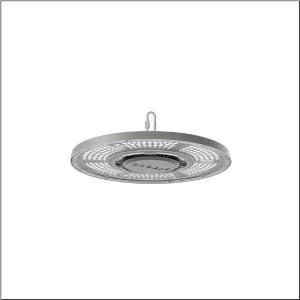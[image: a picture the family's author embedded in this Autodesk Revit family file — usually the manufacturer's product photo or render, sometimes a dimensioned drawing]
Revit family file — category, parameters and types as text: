
# Revit family: highbay_31-s_51hc42da4fmb
name_source: partatom
category: Lighting Fixtures
units: mm (PartAtom-declared; Revit-internal decimal feet)

## family parameters
Cut with Voids When Loaded = No
Host = Face
Light Source = No
Part Type = Normal
Room Calculation Point = No
Round Connector Dimension = Use Diameter
Shared = No

## types (1)
- Highbay 31-S (1 x LED, 14000 lm, 94 W, 4000K)
    Apparent Load = 94 VA
    CIE Flux Codes = 77 99 100 100 100
    Color Rendering = 80
    Color Temperature = 4000K
    Default Elevation = 1800 mm
    Description = Highbay 31-S, LED high bay luminaire, primary light control with lens, of PC, primary optical cover: cover panel, of PC, transparent, light emission: direct distribution, primary light characteristic: rotationally symmetric, installation type: suspended mounting, surface-mounted, LED, rated luminous flux: 14.000lm, luminous efficacy: 150lm/W, light colour: 840, colour temperature: 4000K, control gear: ECG DALI, with cable, 5x 1.0mm², free wire ends, mains connection: 220..240V, AC/DC, 0/50..60Hz, cable length: 1,5m, rated input power: 94W, housing, rotationally symmetric, of diecast aluminium, powder-coated, grey aluminium (RAL 9007), with hook on luminaire side, incl. screw, diameter: 339mm, protection rating (complete): IP65, insulation class (complete): insulation class I (protective earthing), certification: CE, ENEC, UKCA, protection symbol: D, impact resistance: IK08, permissible operating ambient temperature: -30..+45°C, standard: EN 60598-2-22, EN 60598, corresponds to IFS (International Featured Standards) requirements for safety and quality in the food industry, packaging unit: 1 piece
    Height = 141 mm
    Lamp = 1 x LED
    Lamp Light Flux = 14000 lm
    Lamp Power = 94 W
    Lamp count = 1
    Length = 339 mm
    Luminous efficacy = 149 lm/W
    Manufacturer = Siteco
    ModVariant = No
    Model = 51HC42DA4FMB
    Mounting Place = Ceiling
    Mounting Type = Pendant
    Number of Poles = 1
    OnlyDefault = Yes
    Power Factor = 1
    Product Name = Highbay 31-S
    Product group = LED high bay luminaire
    ProductGroupID = 903
    Protection Class = Protection class I
    Protection Degree = IP 65
    RLX_Detail_Level = 1
    RLX_Emergency_Light_Flux = 0 lm
    RLX_Emergency_Type = 0
    RLX_Emergency_Type_DB = No
    RlxData = <blob elided: 162549 chars, md5=4f420138>
    Socket = socket
    Standby Power = 0 W
    System Light Flux = 14000 lm
    System Power = 94 W
    Type Comments = Product without accessories
    Type Image = l_1007237.jpg
    URL = http://relux.com
    VarID = ---
    Voltage = 0 V
    Weight = 0.00 kg
    Width = 0 mm  [stored 0 ft]

note: [stored X ft] marks values corroborated as IEEE doubles in the binary element streams (Revit-internal decimal feet)

## geometry (parser evidence)
native form markers: Blend x4, Sweep x9
no freeform markers — native parametric forms only
